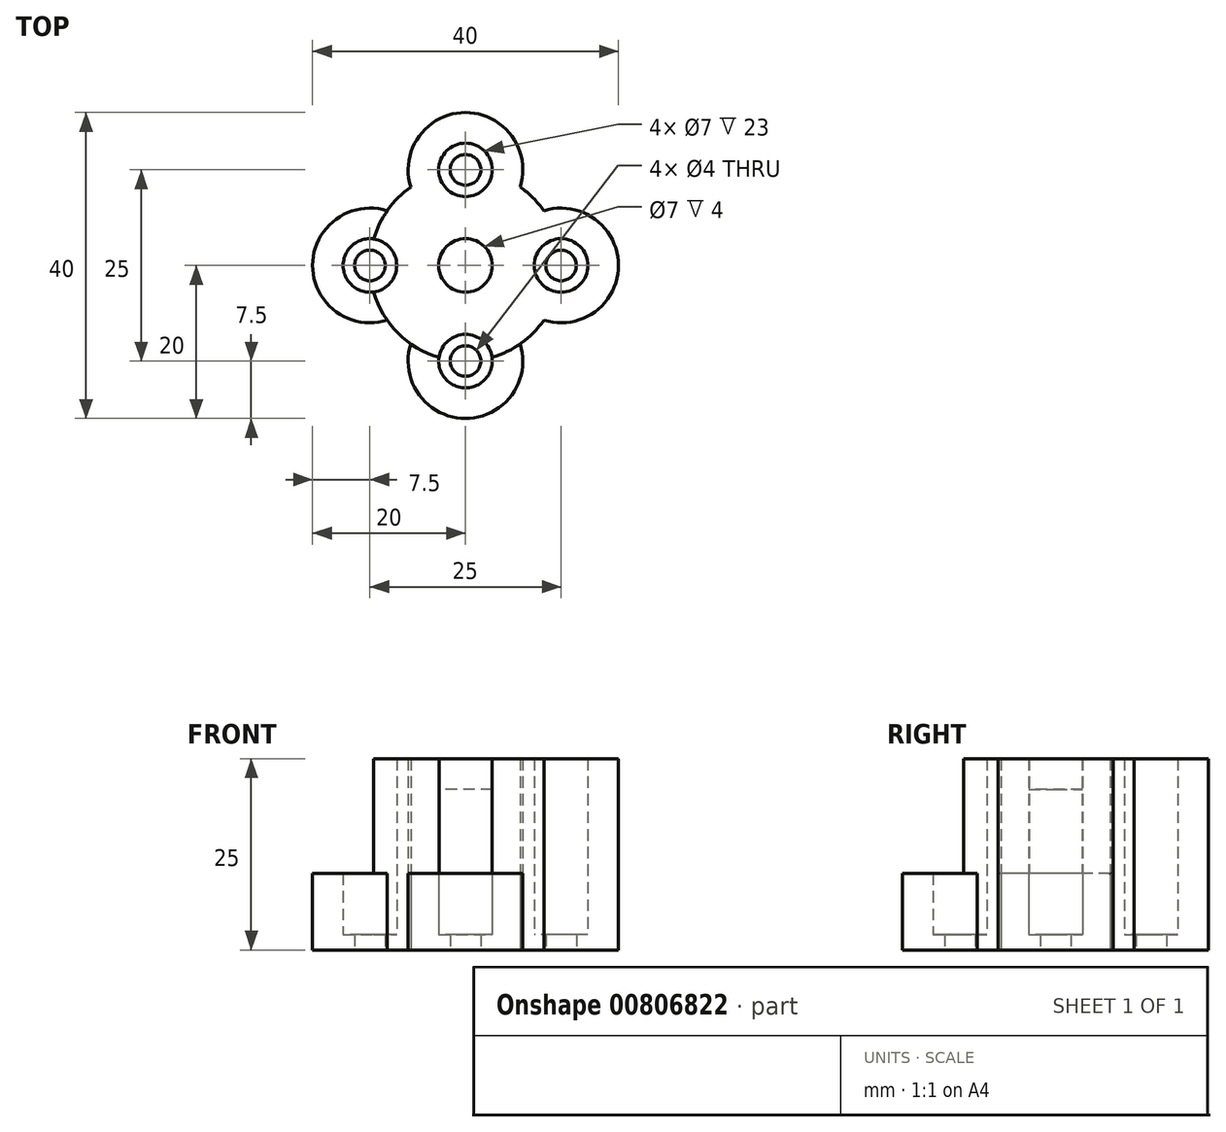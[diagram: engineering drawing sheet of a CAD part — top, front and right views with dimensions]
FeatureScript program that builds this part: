
annotation { "Feature Type Name" : "Feature", "Feature Type Description" : "" }
export const myFeature = defineFeature(function(context is Context, id is Id, definition is map)
    precondition{}
    {
        {
            var Q0;
            Q0=qCreatedBy(makeId("Top.planeOp"),FACE);
            var sketch = newSketch(context, id + "F0", { "sketchPlane" : qUnion([Q0])});
            skCircle(sketch, "E0", {"center": v(0, 0) * mm, "radius": 12.5 * mm});
            skCircle(sketch, "E1", {"center": v(0, 0) * mm, "radius": 3.5 * mm});
            skCircle(sketch, "E2", {"center": v(0, -12.5) * mm, "radius": 7.5 * mm});
            skCircle(sketch, "E3", {"center": v(0, 12.5) * mm, "radius": 7.5 * mm});
            skCircle(sketch, "E4", {"center": v(12.5, 0) * mm, "radius": 7.5 * mm});
            skCircle(sketch, "E5", {"center": v(-12.5, 0) * mm, "radius": 7.5 * mm});
            skCircle(sketch, "E6", {"center": v(-12.5, 0) * mm, "radius": 3.5 * mm});
            skCircle(sketch, "E7", {"center": v(0, 12.5) * mm, "radius": 3.5 * mm});
            skCircle(sketch, "E8", {"center": v(12.5, 0) * mm, "radius": 3.5 * mm});
            skCircle(sketch, "E9", {"center": v(0, -12.5) * mm, "radius": 3.5 * mm});
            skCircle(sketch, "E10", {"center": v(-12.5, 0) * mm, "radius": 2 * mm});
            skCircle(sketch, "E11", {"center": v(0, 12.5) * mm, "radius": 2 * mm});
            skCircle(sketch, "E12", {"center": v(12.5, 0) * mm, "radius": 2 * mm});
            skCircle(sketch, "E13", {"center": v(0, -12.5) * mm, "radius": 2 * mm});
            skSolve(sketch);
        }
        {
            var Q0;
            Q0=makeQuery(id+"F0.imprint","IMPRINT",FACE,{"disambiguationData":[TD([[makeQuery(id+"F0.imprint","IMPRINT",EDGE,{"derivedFrom":sQuery(id+"F0.wireOp",EDGE,"E1")}),-1.0]])]});
            var Q1;
            {var subQ0=sQuery(id+"F0.wireOp",EDGE,"E3");var subQ1=sQuery(id+"F0.wireOp",EDGE,"E0");var subQ2=makeQuery(id+"F0.imprint","INTERSECT",VERTEX,{"disambiguationData":[OD(0.0)],"derivedFrom":[subQ1,subQ0]});Q1=makeQuery(id+"F0.imprint","IMPRINT",FACE,{"disambiguationData":[TD([[makeQuery(id+"F0.imprint","IMPRINT",EDGE,{"disambiguationData":[TD([[subQ2,-1.0]])],"derivedFrom":subQ1}),1.0]])]});}
            var Q2;
            {var subQ0=sQuery(id+"F0.wireOp",EDGE,"E5");var subQ1=sQuery(id+"F0.wireOp",EDGE,"E0");var subQ2=makeQuery(id+"F0.imprint","INTERSECT",VERTEX,{"disambiguationData":[OD(0.0)],"derivedFrom":[subQ1,subQ0]});Q2=makeQuery(id+"F0.imprint","IMPRINT",FACE,{"disambiguationData":[TD([[makeQuery(id+"F0.imprint","IMPRINT",EDGE,{"disambiguationData":[TD([[subQ2,-1.0]])],"derivedFrom":subQ1}),1.0]])]});}
            var Q3;
            {var subQ0=sQuery(id+"F0.wireOp",EDGE,"E2");var subQ1=sQuery(id+"F0.wireOp",EDGE,"E0");var subQ2=makeQuery(id+"F0.imprint","INTERSECT",VERTEX,{"disambiguationData":[OD(0.0)],"derivedFrom":[subQ1,subQ0]});Q3=makeQuery(id+"F0.imprint","IMPRINT",FACE,{"disambiguationData":[TD([[makeQuery(id+"F0.imprint","IMPRINT",EDGE,{"disambiguationData":[TD([[subQ2,-1.0]])],"derivedFrom":subQ1}),1.0]])]});}
            var Q4;
            {var subQ0=sQuery(id+"F0.wireOp",EDGE,"E4");var subQ1=sQuery(id+"F0.wireOp",EDGE,"E0");var subQ2=makeQuery(id+"F0.imprint","INTERSECT",VERTEX,{"disambiguationData":[OD(0.0)],"derivedFrom":[subQ1,subQ0]});Q4=makeQuery(id+"F0.imprint","IMPRINT",FACE,{"disambiguationData":[TD([[makeQuery(id+"F0.imprint","IMPRINT",EDGE,{"disambiguationData":[TD([[subQ2,1.0]])],"derivedFrom":subQ1}),1.0]])]});}
            var Q5;
            {var subQ0=sQuery(id+"F0.wireOp",EDGE,"E4");var subQ1=sQuery(id+"F0.wireOp",EDGE,"E0");var subQ2=makeQuery(id+"F0.imprint","INTERSECT",VERTEX,{"disambiguationData":[OD(0.0)],"derivedFrom":[subQ1,subQ0]});Q5=makeQuery(id+"F0.imprint","IMPRINT",FACE,{"disambiguationData":[TD([[makeQuery(id+"F0.imprint","IMPRINT",EDGE,{"disambiguationData":[TD([[subQ2,1.0]])],"derivedFrom":subQ1}),-1.0]])]});}
            var Q6;
            {var subQ0=sQuery(id+"F0.wireOp",EDGE,"E3");var subQ1=sQuery(id+"F0.wireOp",EDGE,"E0");var subQ2=makeQuery(id+"F0.imprint","INTERSECT",VERTEX,{"disambiguationData":[OD(0.0)],"derivedFrom":[subQ1,subQ0]});Q6=makeQuery(id+"F0.imprint","IMPRINT",FACE,{"disambiguationData":[TD([[makeQuery(id+"F0.imprint","IMPRINT",EDGE,{"disambiguationData":[TD([[subQ2,-1.0]])],"derivedFrom":subQ1}),-1.0]])]});}
            extrude(context, id + "F1", {"entities" : qUnion([Q0, Q1, Q2, Q3, Q4, Q5, Q6]), "depth" : 25 * mm, "offsetDistance" : 25 * mm});
        }
        {
            var Q0;
            {var subQ0=sQuery(id+"F0.wireOp",EDGE,"E9");var subQ1=sQuery(id+"F0.wireOp",EDGE,"E0");var subQ2=makeQuery(id+"F0.imprint","INTERSECT",VERTEX,{"disambiguationData":[OD(0.0)],"derivedFrom":[subQ1,subQ0]});Q0=makeQuery(id+"F0.imprint","IMPRINT",FACE,{"disambiguationData":[TD([[makeQuery(id+"F0.imprint","IMPRINT",EDGE,{"disambiguationData":[TD([[subQ2,-1.0]])],"derivedFrom":subQ1}),-1.0]])]});}
            var Q1;
            {var subQ0=sQuery(id+"F0.wireOp",EDGE,"E9");var subQ1=sQuery(id+"F0.wireOp",EDGE,"E0");var subQ2=makeQuery(id+"F0.imprint","INTERSECT",VERTEX,{"disambiguationData":[OD(0.0)],"derivedFrom":[subQ1,subQ0]});Q1=makeQuery(id+"F0.imprint","IMPRINT",FACE,{"disambiguationData":[TD([[makeQuery(id+"F0.imprint","IMPRINT",EDGE,{"disambiguationData":[TD([[subQ2,-1.0]])],"derivedFrom":subQ1}),1.0]])]});}
            var Q2;
            {var subQ0=sQuery(id+"F0.wireOp",EDGE,"E6");var subQ1=sQuery(id+"F0.wireOp",EDGE,"E0");var subQ2=makeQuery(id+"F0.imprint","INTERSECT",VERTEX,{"disambiguationData":[OD(0.0)],"derivedFrom":[subQ1,subQ0]});Q2=makeQuery(id+"F0.imprint","IMPRINT",FACE,{"disambiguationData":[TD([[makeQuery(id+"F0.imprint","IMPRINT",EDGE,{"disambiguationData":[TD([[subQ2,-1.0]])],"derivedFrom":subQ1}),-1.0]])]});}
            var Q3;
            {var subQ0=sQuery(id+"F0.wireOp",EDGE,"E6");var subQ1=sQuery(id+"F0.wireOp",EDGE,"E0");var subQ2=makeQuery(id+"F0.imprint","INTERSECT",VERTEX,{"disambiguationData":[OD(0.0)],"derivedFrom":[subQ1,subQ0]});Q3=makeQuery(id+"F0.imprint","IMPRINT",FACE,{"disambiguationData":[TD([[makeQuery(id+"F0.imprint","IMPRINT",EDGE,{"disambiguationData":[TD([[subQ2,-1.0]])],"derivedFrom":subQ1}),1.0]])]});}
            var Q4;
            {var subQ0=sQuery(id+"F0.wireOp",EDGE,"E7");var subQ1=sQuery(id+"F0.wireOp",EDGE,"E0");var subQ2=makeQuery(id+"F0.imprint","INTERSECT",VERTEX,{"disambiguationData":[OD(0.0)],"derivedFrom":[subQ1,subQ0]});Q4=makeQuery(id+"F0.imprint","IMPRINT",FACE,{"disambiguationData":[TD([[makeQuery(id+"F0.imprint","IMPRINT",EDGE,{"disambiguationData":[TD([[subQ2,-1.0]])],"derivedFrom":subQ1}),-1.0]])]});}
            var Q5;
            {var subQ0=sQuery(id+"F0.wireOp",EDGE,"E7");var subQ1=sQuery(id+"F0.wireOp",EDGE,"E0");var subQ2=makeQuery(id+"F0.imprint","INTERSECT",VERTEX,{"disambiguationData":[OD(0.0)],"derivedFrom":[subQ1,subQ0]});Q5=makeQuery(id+"F0.imprint","IMPRINT",FACE,{"disambiguationData":[TD([[makeQuery(id+"F0.imprint","IMPRINT",EDGE,{"disambiguationData":[TD([[subQ2,-1.0]])],"derivedFrom":subQ1}),1.0]])]});}
            var Q6;
            {var subQ0=sQuery(id+"F0.wireOp",EDGE,"E8");var subQ1=sQuery(id+"F0.wireOp",EDGE,"E0");var subQ2=makeQuery(id+"F0.imprint","INTERSECT",VERTEX,{"disambiguationData":[OD(0.0)],"derivedFrom":[subQ1,subQ0]});Q6=makeQuery(id+"F0.imprint","IMPRINT",FACE,{"disambiguationData":[TD([[makeQuery(id+"F0.imprint","IMPRINT",EDGE,{"disambiguationData":[TD([[subQ2,1.0]])],"derivedFrom":subQ1}),-1.0]])]});}
            var Q7;
            {var subQ0=sQuery(id+"F0.wireOp",EDGE,"E8");var subQ1=sQuery(id+"F0.wireOp",EDGE,"E0");var subQ2=makeQuery(id+"F0.imprint","INTERSECT",VERTEX,{"disambiguationData":[OD(0.0)],"derivedFrom":[subQ1,subQ0]});Q7=makeQuery(id+"F0.imprint","IMPRINT",FACE,{"disambiguationData":[TD([[makeQuery(id+"F0.imprint","IMPRINT",EDGE,{"disambiguationData":[TD([[subQ2,1.0]])],"derivedFrom":subQ1}),1.0]])]});}
            extrude(context, id + "F2", {"entities" : qUnion([Q0, Q1, Q2, Q3, Q4, Q5, Q6, Q7]), "operationType" : NewBodyOperationType.ADD, "depth" : 2 * mm, "offsetDistance" : 25 * mm});
        }
        {
            var Q0;
            {var subQ0=sQuery(id+"F0.wireOp",EDGE,"E5");var subQ1=sQuery(id+"F0.wireOp",EDGE,"E0");var subQ2=makeQuery(id+"F0.imprint","INTERSECT",VERTEX,{"disambiguationData":[OD(0.0)],"derivedFrom":[subQ1,subQ0]});Q0=makeQuery(id+"F0.imprint","IMPRINT",FACE,{"disambiguationData":[TD([[makeQuery(id+"F0.imprint","IMPRINT",EDGE,{"disambiguationData":[TD([[subQ2,-1.0]])],"derivedFrom":subQ1}),-1.0]])]});}
            var Q1;
            {var subQ0=sQuery(id+"F0.wireOp",EDGE,"E2");var subQ1=sQuery(id+"F0.wireOp",EDGE,"E0");var subQ2=makeQuery(id+"F0.imprint","INTERSECT",VERTEX,{"disambiguationData":[OD(0.0)],"derivedFrom":[subQ1,subQ0]});Q1=makeQuery(id+"F0.imprint","IMPRINT",FACE,{"disambiguationData":[TD([[makeQuery(id+"F0.imprint","IMPRINT",EDGE,{"disambiguationData":[TD([[subQ2,-1.0]])],"derivedFrom":subQ1}),-1.0]])]});}
            extrude(context, id + "F3", {"entities" : qUnion([Q0, Q1]), "operationType" : NewBodyOperationType.ADD, "depth" : 10 * mm, "offsetDistance" : 25 * mm});
        }
        {
            var Q0;
            Q0=makeQuery(id+"F0.imprint","IMPRINT",FACE,{"disambiguationData":[TD([[makeQuery(id+"F0.imprint","IMPRINT",EDGE,{"derivedFrom":sQuery(id+"F0.wireOp",EDGE,"E1")}),1.0]])]});
            extrude(context, id + "F4", {"entities" : qUnion([Q0]), "operationType" : NewBodyOperationType.ADD, "depth" : 21 * mm, "offsetDistance" : 25 * mm});
        }
    });
